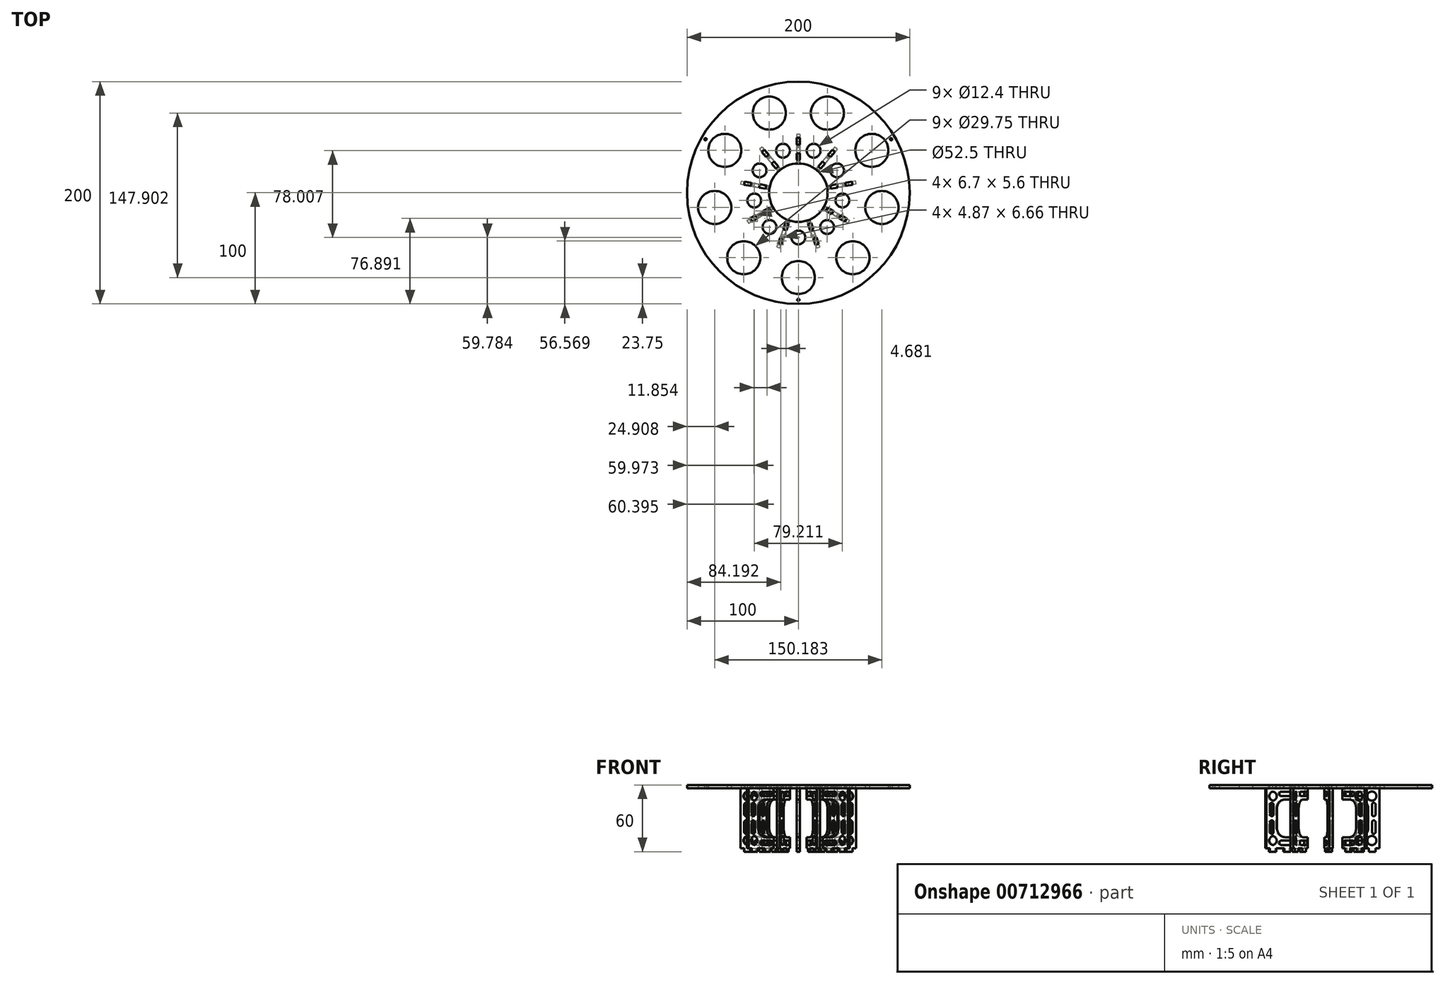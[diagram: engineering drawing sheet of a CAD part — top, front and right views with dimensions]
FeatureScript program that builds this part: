
annotation { "Feature Type Name" : "Feature", "Feature Type Description" : "" }
export const myFeature = defineFeature(function(context is Context, id is Id, definition is map)
    precondition{}
    {
        {
            assignVariable(context, id + "F0", {"name" : "flange_thickness", "anyValue" : 3});
        }
        {
            var Q0;
            Q0=qCreatedBy(makeId("Top.planeOp"),FACE);
            var sketch = newSketch(context, id + "F1", { "sketchPlane" : qUnion([Q0])});
            skLineSegment(sketch, "E0", {"start": v(0, 59.67) * mm, "end": v(0, 52.5) * mm, "construction": true});
            skLineSegment(sketch, "E1", {"start": v(-66.4, 0) * mm, "end": v(93.75, 0) * mm, "construction": true});
            skCircle(sketch, "E2", {"center": v(0, 0) * mm, "radius": 26.25 * mm});
            skCircle(sketch, "E3", {"center": v(0, 0) * mm, "radius": 52.5 * mm});
            skCircle(sketch, "E4", {"center": v(0, 0) * mm, "radius": 100 * mm});
            skLineSegment(sketch, "E5", {"start": v(-52.82, 0) * mm, "end": v(20.55, 0) * mm, "construction": true});
            skLineSegment(sketch, "E6.MirrorCS", {"start": v(1.5, 35.53) * mm, "end": v(1.5, 29.53) * mm});
            skLineSegment(sketch, "E7.MirrorCS", {"start": v(1.5, 49.22) * mm, "end": v(1.5, 43.22) * mm});
            skLineSegment(sketch, "E8.MirrorCS", {"start": v(-1.5, 49.22) * mm, "end": v(-1.5, 43.22) * mm});
            skLineSegment(sketch, "E9", {"start": v(1.5, 49.22) * mm, "end": v(-1.5, 49.22) * mm});
            skLineSegment(sketch, "E10", {"start": v(1.5, 43.22) * mm, "end": v(-1.5, 43.22) * mm});
            skLineSegment(sketch, "E11.MirrorCS", {"start": v(-1.5, 35.53) * mm, "end": v(-1.5, 29.53) * mm});
            skLineSegment(sketch, "E12", {"start": v(1.5, 29.53) * mm, "end": v(-1.5, 29.53) * mm});
            skLineSegment(sketch, "E13", {"start": v(1.5, 35.53) * mm, "end": v(-1.5, 35.53) * mm});
            skLineSegment(sketch, "E14", {"start": v(0, 52.5) * mm, "end": v(0, 26.25) * mm, "construction": true});
            skLineSegment(sketch, "E15", {"start": v(0, 26.25) * mm, "end": v(0, -100) * mm, "construction": true});
            skLineSegment(sketch, "E16.1.0", {"start": v(-21.69, 28.18) * mm, "end": v(-17.83, 23.59) * mm});
            skLineSegment(sketch, "E16.1.1", {"start": v(-23.99, 26.25) * mm, "end": v(-20.13, 21.66) * mm});
            skLineSegment(sketch, "E16.1.2", {"start": v(-17.83, 23.59) * mm, "end": v(-20.13, 21.66) * mm});
            skLineSegment(sketch, "E16.1.3", {"start": v(-21.69, 28.18) * mm, "end": v(-23.99, 26.25) * mm});
            skLineSegment(sketch, "E16.1.4", {"start": v(-26.63, 34.07) * mm, "end": v(-28.93, 32.14) * mm});
            skLineSegment(sketch, "E16.1.5", {"start": v(-30.49, 38.67) * mm, "end": v(-26.63, 34.07) * mm});
            skLineSegment(sketch, "E16.1.6", {"start": v(-32.79, 36.74) * mm, "end": v(-28.93, 32.14) * mm});
            skLineSegment(sketch, "E16.1.7", {"start": v(-30.49, 38.67) * mm, "end": v(-32.79, 36.74) * mm});
            skLineSegment(sketch, "E16.2.0", {"start": v(-34.73, 7.65) * mm, "end": v(-28.82, 6.6) * mm});
            skLineSegment(sketch, "E16.2.1", {"start": v(-35.25, 4.7) * mm, "end": v(-29.34, 3.65) * mm});
            skLineSegment(sketch, "E16.2.2", {"start": v(-28.82, 6.6) * mm, "end": v(-29.34, 3.65) * mm});
            skLineSegment(sketch, "E16.2.3", {"start": v(-34.73, 7.65) * mm, "end": v(-35.25, 4.7) * mm});
            skLineSegment(sketch, "E16.2.4", {"start": v(-42.3, 8.98) * mm, "end": v(-42.82, 6.03) * mm});
            skLineSegment(sketch, "E16.2.5", {"start": v(-48.21, 10.02) * mm, "end": v(-42.3, 8.98) * mm});
            skLineSegment(sketch, "E16.2.6", {"start": v(-48.73, 7.07) * mm, "end": v(-42.82, 6.03) * mm});
            skLineSegment(sketch, "E16.2.7", {"start": v(-48.21, 10.02) * mm, "end": v(-48.73, 7.07) * mm});
            skLineSegment(sketch, "E16.3.0", {"start": v(-31.52, -16.47) * mm, "end": v(-26.32, -13.47) * mm});
            skLineSegment(sketch, "E16.3.1", {"start": v(-30.02, -19.06) * mm, "end": v(-24.82, -16.06) * mm});
            skLineSegment(sketch, "E16.3.2", {"start": v(-26.32, -13.47) * mm, "end": v(-24.82, -16.06) * mm});
            skLineSegment(sketch, "E16.3.3", {"start": v(-31.52, -16.47) * mm, "end": v(-30.02, -19.06) * mm});
            skLineSegment(sketch, "E16.3.4", {"start": v(-38.18, -20.31) * mm, "end": v(-36.68, -22.9) * mm});
            skLineSegment(sketch, "E16.3.5", {"start": v(-43.37, -23.31) * mm, "end": v(-38.18, -20.31) * mm});
            skLineSegment(sketch, "E16.3.6", {"start": v(-41.87, -25.9) * mm, "end": v(-36.68, -22.9) * mm});
            skLineSegment(sketch, "E16.3.7", {"start": v(-43.37, -23.31) * mm, "end": v(-41.87, -25.9) * mm});
            skLineSegment(sketch, "E16.4.0", {"start": v(-13.56, -32.88) * mm, "end": v(-11.5, -27.24) * mm});
            skLineSegment(sketch, "E16.4.1", {"start": v(-10.74, -33.9) * mm, "end": v(-8.7, -28.26) * mm});
            skLineSegment(sketch, "E16.4.2", {"start": v(-11.5, -27.24) * mm, "end": v(-8.7, -28.26) * mm});
            skLineSegment(sketch, "E16.4.3", {"start": v(-13.56, -32.88) * mm, "end": v(-10.74, -33.9) * mm});
            skLineSegment(sketch, "E16.4.4", {"start": v(-16.2, -40.1) * mm, "end": v(-13.37, -41.13) * mm});
            skLineSegment(sketch, "E16.4.5", {"start": v(-18.24, -45.74) * mm, "end": v(-16.2, -40.1) * mm});
            skLineSegment(sketch, "E16.4.6", {"start": v(-15.42, -46.76) * mm, "end": v(-13.37, -41.13) * mm});
            skLineSegment(sketch, "E16.4.7", {"start": v(-18.24, -45.74) * mm, "end": v(-15.42, -46.76) * mm});
            skLineSegment(sketch, "E16.5.0", {"start": v(10.74, -33.9) * mm, "end": v(8.7, -28.26) * mm});
            skLineSegment(sketch, "E16.5.1", {"start": v(13.56, -32.88) * mm, "end": v(11.5, -27.24) * mm});
            skLineSegment(sketch, "E16.5.2", {"start": v(8.7, -28.26) * mm, "end": v(11.5, -27.24) * mm});
            skLineSegment(sketch, "E16.5.3", {"start": v(10.74, -33.9) * mm, "end": v(13.56, -32.88) * mm});
            skLineSegment(sketch, "E16.5.4", {"start": v(13.37, -41.13) * mm, "end": v(16.2, -40.1) * mm});
            skLineSegment(sketch, "E16.5.5", {"start": v(15.42, -46.76) * mm, "end": v(13.37, -41.13) * mm});
            skLineSegment(sketch, "E16.5.6", {"start": v(18.24, -45.74) * mm, "end": v(16.2, -40.1) * mm});
            skLineSegment(sketch, "E16.5.7", {"start": v(15.42, -46.76) * mm, "end": v(18.24, -45.74) * mm});
            skLineSegment(sketch, "E16.6.0", {"start": v(30.02, -19.06) * mm, "end": v(24.82, -16.06) * mm});
            skLineSegment(sketch, "E16.6.1", {"start": v(31.52, -16.47) * mm, "end": v(26.32, -13.47) * mm});
            skLineSegment(sketch, "E16.6.2", {"start": v(24.82, -16.06) * mm, "end": v(26.32, -13.47) * mm});
            skLineSegment(sketch, "E16.6.3", {"start": v(30.02, -19.06) * mm, "end": v(31.52, -16.47) * mm});
            skLineSegment(sketch, "E16.6.4", {"start": v(36.68, -22.9) * mm, "end": v(38.18, -20.31) * mm});
            skLineSegment(sketch, "E16.6.5", {"start": v(41.87, -25.9) * mm, "end": v(36.68, -22.9) * mm});
            skLineSegment(sketch, "E16.6.6", {"start": v(43.37, -23.31) * mm, "end": v(38.18, -20.31) * mm});
            skLineSegment(sketch, "E16.6.7", {"start": v(41.87, -25.9) * mm, "end": v(43.37, -23.31) * mm});
            skLineSegment(sketch, "E16.7.0", {"start": v(35.25, 4.7) * mm, "end": v(29.34, 3.65) * mm});
            skLineSegment(sketch, "E16.7.1", {"start": v(34.73, 7.65) * mm, "end": v(28.82, 6.6) * mm});
            skLineSegment(sketch, "E16.7.2", {"start": v(29.34, 3.65) * mm, "end": v(28.82, 6.6) * mm});
            skLineSegment(sketch, "E16.7.3", {"start": v(35.25, 4.7) * mm, "end": v(34.73, 7.65) * mm});
            skLineSegment(sketch, "E16.7.4", {"start": v(42.82, 6.03) * mm, "end": v(42.3, 8.98) * mm});
            skLineSegment(sketch, "E16.7.5", {"start": v(48.73, 7.07) * mm, "end": v(42.82, 6.03) * mm});
            skLineSegment(sketch, "E16.7.6", {"start": v(48.21, 10.02) * mm, "end": v(42.3, 8.98) * mm});
            skLineSegment(sketch, "E16.7.7", {"start": v(48.73, 7.07) * mm, "end": v(48.21, 10.02) * mm});
            skLineSegment(sketch, "E16.8.0", {"start": v(23.99, 26.25) * mm, "end": v(20.13, 21.66) * mm});
            skLineSegment(sketch, "E16.8.1", {"start": v(21.69, 28.18) * mm, "end": v(17.83, 23.59) * mm});
            skLineSegment(sketch, "E16.8.2", {"start": v(20.13, 21.66) * mm, "end": v(17.83, 23.59) * mm});
            skLineSegment(sketch, "E16.8.3", {"start": v(23.99, 26.25) * mm, "end": v(21.69, 28.18) * mm});
            skLineSegment(sketch, "E16.8.4", {"start": v(28.93, 32.14) * mm, "end": v(26.63, 34.07) * mm});
            skLineSegment(sketch, "E16.8.5", {"start": v(32.79, 36.74) * mm, "end": v(28.93, 32.14) * mm});
            skLineSegment(sketch, "E16.8.6", {"start": v(30.49, 38.67) * mm, "end": v(26.63, 34.07) * mm});
            skLineSegment(sketch, "E16.8.7", {"start": v(32.79, 36.74) * mm, "end": v(30.49, 38.67) * mm});
            skCircle(sketch, "E17", {"center": v(0, -40.22) * mm, "radius": 6.2 * mm});
            skCircle(sketch, "E18", {"center": v(0, -76.25) * mm, "radius": 14.87 * mm});
            skCircle(sketch, "E19.1.0", {"center": v(49.01, -58.41) * mm, "radius": 14.87 * mm});
            skCircle(sketch, "E19.1.1", {"center": v(25.85, -30.8) * mm, "radius": 6.2 * mm});
            skCircle(sketch, "E19.2.0", {"center": v(75.1, -13.24) * mm, "radius": 14.87 * mm});
            skCircle(sketch, "E19.2.1", {"center": v(39.6, -6.98) * mm, "radius": 6.2 * mm});
            skCircle(sketch, "E19.3.0", {"center": v(66.03, 38.13) * mm, "radius": 14.87 * mm});
            skCircle(sketch, "E19.3.1", {"center": v(34.83, 20.1) * mm, "radius": 6.2 * mm});
            skCircle(sketch, "E19.4.0", {"center": v(26.08, 71.65) * mm, "radius": 14.87 * mm});
            skCircle(sketch, "E19.4.1", {"center": v(13.75, 37.8) * mm, "radius": 6.2 * mm});
            skCircle(sketch, "E19.5.0", {"center": v(-26.08, 71.65) * mm, "radius": 14.87 * mm});
            skCircle(sketch, "E19.5.1", {"center": v(-13.75, 37.8) * mm, "radius": 6.2 * mm});
            skCircle(sketch, "E19.6.0", {"center": v(-66.03, 38.13) * mm, "radius": 14.87 * mm});
            skCircle(sketch, "E19.6.1", {"center": v(-34.83, 20.1) * mm, "radius": 6.2 * mm});
            skCircle(sketch, "E19.7.0", {"center": v(-75.1, -13.24) * mm, "radius": 14.87 * mm});
            skCircle(sketch, "E19.7.1", {"center": v(-39.6, -6.98) * mm, "radius": 6.2 * mm});
            skCircle(sketch, "E19.8.0", {"center": v(-49.01, -58.41) * mm, "radius": 14.87 * mm});
            skCircle(sketch, "E19.8.1", {"center": v(-25.85, -30.8) * mm, "radius": 6.2 * mm});
            skCircle(sketch, "E20", {"center": v(0, -96.3) * mm, "radius": 1 * mm});
            skCircle(sketch, "E21.1.0", {"center": v(83.4, 48.15) * mm, "radius": 1 * mm});
            skCircle(sketch, "E21.2.0", {"center": v(-83.4, 48.15) * mm, "radius": 1 * mm});
            skSolve(sketch);
        }
        {
            var Q0;
            Q0=qCreatedBy(makeId("Right.planeOp"),FACE);
            var sketch = newSketch(context, id + "F2", { "sketchPlane" : qUnion([Q0])});
            skLineSegment(sketch, "E22", {"start": v(52.5, 0) * mm, "end": v(52.5, -27) * mm});
            skLineSegment(sketch, "E23", {"start": v(26.25, 0) * mm, "end": v(26.25, -10) * mm});
            skLineSegment(sketch, "E24", {"start": v(0, 0) * mm, "end": v(0, -73.37) * mm, "construction": true});
            skLineSegment(sketch, "E25", {"start": v(52.5, 0) * mm, "end": v(49.22, 0) * mm});
            skLineSegment(sketch, "E26", {"start": v(43.22, 0) * mm, "end": v(35.53, 0) * mm});
            skLineSegment(sketch, "E27", {"start": v(29.53, 0) * mm, "end": v(26.25, 0) * mm});
            skLineSegment(sketch, "E28", {"start": v(49.22, 0) * mm, "end": v(49.22, 3) * mm});
            skLineSegment(sketch, "E29", {"start": v(49.22, 3) * mm, "end": v(43.22, 3) * mm});
            skLineSegment(sketch, "E30", {"start": v(43.22, 3) * mm, "end": v(43.22, 0) * mm});
            skLineSegment(sketch, "E31", {"start": v(35.53, 0) * mm, "end": v(35.53, 3) * mm});
            skLineSegment(sketch, "E32", {"start": v(35.53, 3) * mm, "end": v(29.53, 3) * mm});
            skLineSegment(sketch, "E33", {"start": v(29.53, 3) * mm, "end": v(29.53, 0) * mm});
            skLineSegment(sketch, "E34", {"start": v(26.25, -10) * mm, "end": v(34.5, -10) * mm});
            skLineSegment(sketch, "E35", {"start": v(42.5, -18) * mm, "end": v(42.5, -27) * mm});
            skLineSegment(sketch, "E36", {"start": v(42.5, -27) * mm, "end": v(52.5, -27) * mm});
            skPoint(sketch, "E37.visualSharp", {"position": v(42.5, -10) * mm});
            skArc(sketch, "E37.filletArc", {"start": v(42.5, -18) * mm, "mid": v(40.16, -12.34) * mm, "end": v(34.5, -10) * mm});
            skCircle(sketch, "E38", {"center": v(45.76, -7.04) * mm, "radius": 4.08 * mm});
            skLineSegment(sketch, "E39.left", {"start": v(49.1, -14.68) * mm, "end": v(49.1, -23.5) * mm});
            skLineSegment(sketch, "E39.right", {"start": v(45.9, -14.68) * mm, "end": v(45.9, -23.5) * mm});
            skArc(sketch, "E40", {"start": v(49.1, -14.68) * mm, "mid": v(47.5, -13.07) * mm, "end": v(45.9, -14.68) * mm});
            skArc(sketch, "E41", {"start": v(45.9, -23.5) * mm, "mid": v(47.5, -25.11) * mm, "end": v(49.1, -23.5) * mm});
            skLineSegment(sketch, "E42.left", {"start": v(38.35, -7) * mm, "end": v(29.53, -7) * mm});
            skLineSegment(sketch, "E42.right", {"start": v(38.35, -3) * mm, "end": v(29.53, -3) * mm});
            skArc(sketch, "E43", {"start": v(38.35, -7) * mm, "mid": v(40.34, -5) * mm, "end": v(38.35, -3) * mm});
            skArc(sketch, "E44", {"start": v(29.53, -3) * mm, "mid": v(27.54, -5) * mm, "end": v(29.53, -7) * mm});
            skLineSegment(sketch, "E45", {"start": v(51.53, -27) * mm, "end": v(23.27, -27) * mm, "construction": true});
            skLineSegment(sketch, "E46.MirrorCS", {"start": v(42.5, -36) * mm, "end": v(42.5, -27) * mm});
            skArc(sketch, "E47.MirrorCS", {"start": v(42.5, -36) * mm, "mid": v(40.16, -41.66) * mm, "end": v(34.5, -44) * mm});
            skLineSegment(sketch, "E48.MirrorCS", {"start": v(26.25, -44) * mm, "end": v(34.5, -44) * mm});
            skLineSegment(sketch, "E49.MirrorCS", {"start": v(26.25, -54) * mm, "end": v(26.25, -44) * mm});
            skLineSegment(sketch, "E50.MirrorCS", {"start": v(29.53, -54) * mm, "end": v(26.25, -54) * mm});
            skLineSegment(sketch, "E51.MirrorCS", {"start": v(29.53, -57) * mm, "end": v(29.53, -54) * mm});
            skLineSegment(sketch, "E52.MirrorCS", {"start": v(35.53, -57) * mm, "end": v(29.53, -57) * mm});
            skLineSegment(sketch, "E53.MirrorCS", {"start": v(35.53, -54) * mm, "end": v(35.53, -57) * mm});
            skLineSegment(sketch, "E54.MirrorCS", {"start": v(43.22, -54) * mm, "end": v(35.53, -54) * mm});
            skLineSegment(sketch, "E55.MirrorCS", {"start": v(43.22, -57) * mm, "end": v(43.22, -54) * mm});
            skLineSegment(sketch, "E56.MirrorCS", {"start": v(49.22, -57) * mm, "end": v(43.22, -57) * mm});
            skLineSegment(sketch, "E57.MirrorCS", {"start": v(49.22, -54) * mm, "end": v(49.22, -57) * mm});
            skLineSegment(sketch, "E58.MirrorCS", {"start": v(52.5, -54) * mm, "end": v(49.22, -54) * mm});
            skLineSegment(sketch, "E59.MirrorCS", {"start": v(52.5, -54) * mm, "end": v(52.5, -27) * mm});
            skCircle(sketch, "E60.MirrorC", {"center": v(45.76, -46.96) * mm, "radius": 4.08 * mm});
            skLineSegment(sketch, "E61.MirrorCS", {"start": v(49.1, -39.32) * mm, "end": v(49.1, -30.5) * mm});
            skArc(sketch, "E62.MirrorCS", {"start": v(49.1, -39.32) * mm, "mid": v(47.5, -40.93) * mm, "end": v(45.9, -39.32) * mm});
            skLineSegment(sketch, "E63.MirrorCS", {"start": v(45.9, -39.32) * mm, "end": v(45.9, -30.5) * mm});
            skArc(sketch, "E64.MirrorCS", {"start": v(45.9, -30.5) * mm, "mid": v(47.5, -28.89) * mm, "end": v(49.1, -30.5) * mm});
            skArc(sketch, "E65.MirrorCS", {"start": v(38.35, -47) * mm, "mid": v(40.34, -49) * mm, "end": v(38.35, -51) * mm});
            skLineSegment(sketch, "E66.MirrorCS", {"start": v(38.35, -47) * mm, "end": v(29.53, -47) * mm});
            skLineSegment(sketch, "E67.MirrorCS", {"start": v(38.35, -51) * mm, "end": v(29.53, -51) * mm});
            skArc(sketch, "E68.MirrorCS", {"start": v(29.53, -51) * mm, "mid": v(27.54, -49) * mm, "end": v(29.53, -47) * mm});
            skSolve(sketch);
        }
        {
            var Q0;
            Q0=makeQuery(id+"F1.imprint","IMPRINT",FACE,{"disambiguationData":[TD([[makeQuery(id+"F1.imprint","IMPRINT",EDGE,{"derivedFrom":sQuery(id+"F1.wireOp",EDGE,"E3")}),-1.0]])]});
            var Q1;
            Q1=makeQuery(id+"F1.imprint","IMPRINT",FACE,{"disambiguationData":[TD([[makeQuery(id+"F1.imprint","IMPRINT",EDGE,{"derivedFrom":sQuery(id+"F1.wireOp",EDGE,"E2")}),-1.0]])]});
            extrude(context, id + "F3", {"entities" : qUnion([Q0, Q1]), "depth" : (getVariable(context, 'flange_thickness')) * mm, "offsetDistance" : 25 * mm});
        }
        {
            var Q0;
            Q0=qCreatedBy(makeId("Front.planeOp"),FACE);
            var sketch = newSketch(context, id + "F4", { "sketchPlane" : qUnion([Q0])});
            skLineSegment(sketch, "E69", {"start": v(0, 0) * mm, "end": v(0, -63.74) * mm, "construction": true});
            skSolve(sketch);
        }
        {
            var Q0;
            Q0=makeQuery(id+"F2.imprint","IMPRINT",FACE,{"disambiguationData":[TD([[makeQuery(id+"F2.imprint","IMPRINT",EDGE,{"derivedFrom":sQuery(id+"F2.wireOp",EDGE,"E36")}),-1.0]])]});
            var Q1;
            Q1=makeQuery(id+"F2.imprint","IMPRINT",FACE,{"disambiguationData":[TD([[makeQuery(id+"F2.imprint","IMPRINT",EDGE,{"derivedFrom":sQuery(id+"F2.wireOp",EDGE,"E22")}),-1.0]])]});
            extrude(context, id + "F5", {"entities" : qUnion([Q0, Q1]), "depth" : (getVariable(context, 'flange_thickness')) * mm, "offsetDistance" : 25 * mm, "symmetric" : true});
        }
        {
            var Q0;
            Q0=makeQuery(id+"F5.opExtrude","SWEPT_BODY",BODY,{"disambiguationData":[OSD([sQuery(id+"F2.wireOp",EDGE,"E22"),sQuery(id+"F2.wireOp",EDGE,"E23"),sQuery(id+"F2.wireOp",EDGE,"E25"),sQuery(id+"F2.wireOp",EDGE,"E26"),sQuery(id+"F2.wireOp",EDGE,"E27"),sQuery(id+"F2.wireOp",EDGE,"E28"),sQuery(id+"F2.wireOp",EDGE,"E29"),sQuery(id+"F2.wireOp",EDGE,"E30"),sQuery(id+"F2.wireOp",EDGE,"E31"),sQuery(id+"F2.wireOp",EDGE,"E32"),sQuery(id+"F2.wireOp",EDGE,"E33"),sQuery(id+"F2.wireOp",EDGE,"E34"),sQuery(id+"F2.wireOp",EDGE,"E35"),sQuery(id+"F2.wireOp",EDGE,"E37.filletArc"),sQuery(id+"F2.wireOp",EDGE,"E38"),sQuery(id+"F2.wireOp",EDGE,"E39.left"),sQuery(id+"F2.wireOp",EDGE,"E39.right"),sQuery(id+"F2.wireOp",EDGE,"E40"),sQuery(id+"F2.wireOp",EDGE,"E41"),sQuery(id+"F2.wireOp",EDGE,"E42.left"),sQuery(id+"F2.wireOp",EDGE,"E42.right"),sQuery(id+"F2.wireOp",EDGE,"E43"),sQuery(id+"F2.wireOp",EDGE,"E44"),sQuery(id+"F2.wireOp",EDGE,"E46.MirrorCS"),sQuery(id+"F2.wireOp",EDGE,"E47.MirrorCS"),sQuery(id+"F2.wireOp",EDGE,"E48.MirrorCS"),sQuery(id+"F2.wireOp",EDGE,"E49.MirrorCS"),sQuery(id+"F2.wireOp",EDGE,"E50.MirrorCS"),sQuery(id+"F2.wireOp",EDGE,"E51.MirrorCS"),sQuery(id+"F2.wireOp",EDGE,"E52.MirrorCS"),sQuery(id+"F2.wireOp",EDGE,"E53.MirrorCS"),sQuery(id+"F2.wireOp",EDGE,"E54.MirrorCS"),sQuery(id+"F2.wireOp",EDGE,"E55.MirrorCS"),sQuery(id+"F2.wireOp",EDGE,"E56.MirrorCS"),sQuery(id+"F2.wireOp",EDGE,"E57.MirrorCS"),sQuery(id+"F2.wireOp",EDGE,"E58.MirrorCS"),sQuery(id+"F2.wireOp",EDGE,"E59.MirrorCS"),sQuery(id+"F2.wireOp",EDGE,"E60.MirrorC"),sQuery(id+"F2.wireOp",EDGE,"E61.MirrorCS"),sQuery(id+"F2.wireOp",EDGE,"E62.MirrorCS"),sQuery(id+"F2.wireOp",EDGE,"E63.MirrorCS"),sQuery(id+"F2.wireOp",EDGE,"E64.MirrorCS"),sQuery(id+"F2.wireOp",EDGE,"E65.MirrorCS"),sQuery(id+"F2.wireOp",EDGE,"E66.MirrorCS"),sQuery(id+"F2.wireOp",EDGE,"E67.MirrorCS"),sQuery(id+"F2.wireOp",EDGE,"E68.MirrorCS")])]});
            var Q1;
            Q1=sQuery(id+"F4.wireOp",EDGE,"E69");
            circularPattern(context, id + "F6", {"entities" : qUnion([Q0]), "axis" : qUnion([Q1]), "angle" : 360 * degree, "instanceCount" : 9, "equalSpace" : true, "computeTransformsWithoutBuiltin" : true});
        }
    });
